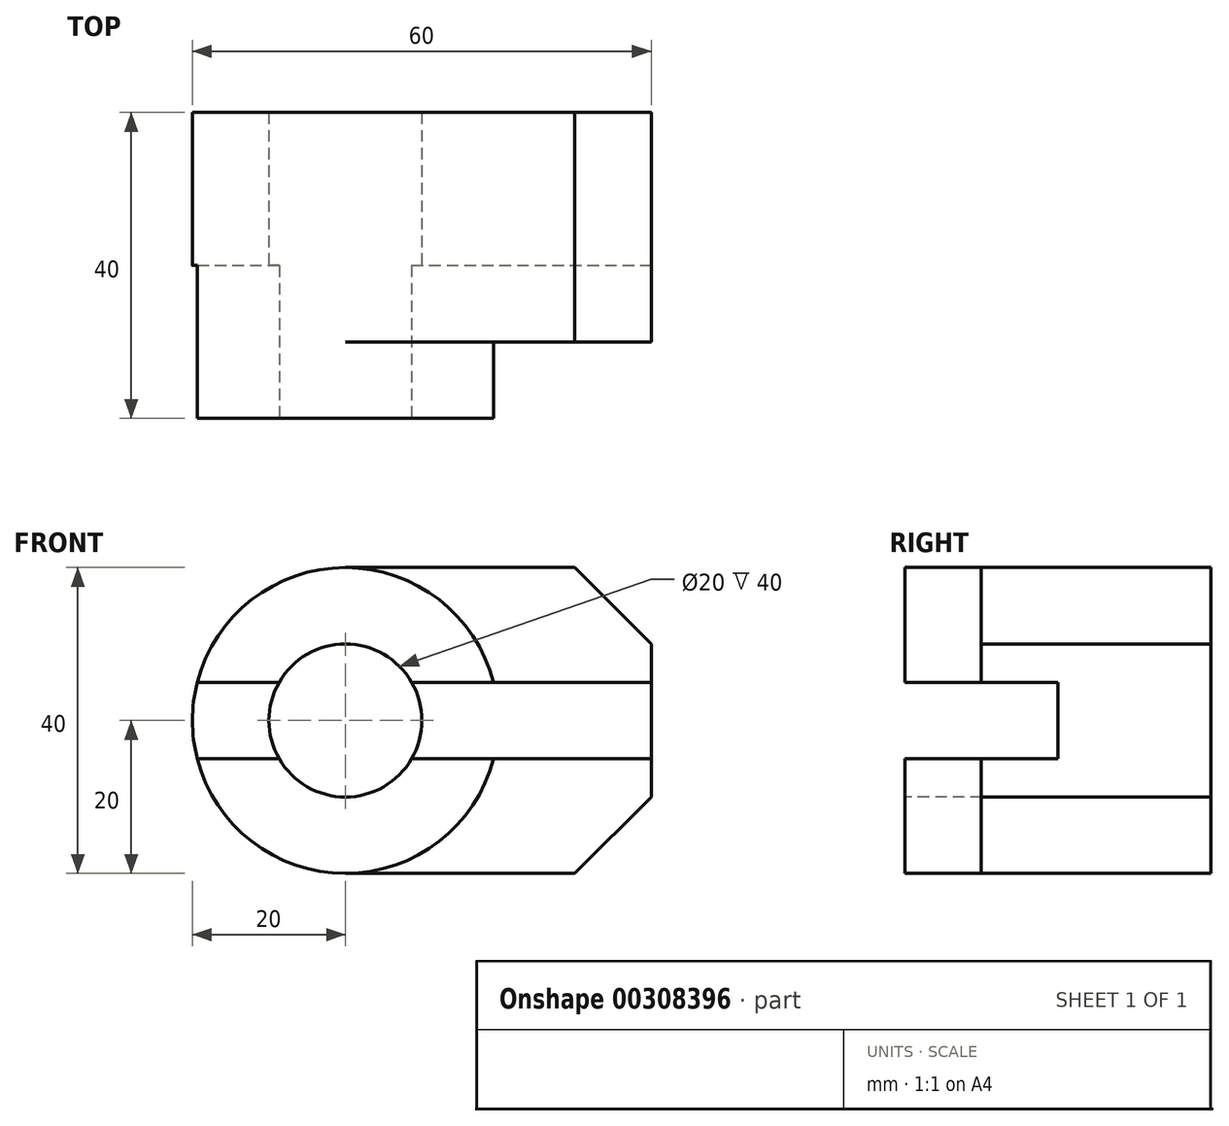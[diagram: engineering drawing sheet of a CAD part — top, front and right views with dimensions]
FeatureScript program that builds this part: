
annotation { "Feature Type Name" : "Feature", "Feature Type Description" : "" }
export const myFeature = defineFeature(function(context is Context, id is Id, definition is map)
    precondition{}
    {
        {
            var Q0;
            Q0=qCreatedBy(makeId("Front.planeOp"),FACE);
            var sketch = newSketch(context, id + "F0", { "sketchPlane" : qUnion([Q0])});
            skCircle(sketch, "E0", {"center": v(0, 0) * mm, "radius": 20 * mm});
            skSolve(sketch);
        }
        {
            var Q0;
            Q0=makeQuery(id+"F0.imprint","IMPRINT",FACE,{"disambiguationData":[TD([[makeQuery(id+"F0.imprint","IMPRINT",EDGE,{"derivedFrom":sQuery(id+"F0.wireOp",EDGE,"E0")}),1.0]])]});
            extrude(context, id + "F1", {"entities" : qUnion([Q0]), "depth" : 40 * mm});
        }
        {
            var Q0;
            Q0=makeQuery(id+"F1.opExtrude","CAP_FACE",FACE,{"disambiguationData":[OSD([sQuery(id+"F0.wireOp",EDGE,"E0")])],"isStart":true});
            var sketch = newSketch(context, id + "F2", { "sketchPlane" : qUnion([Q0])});
            skLineSegment(sketch, "E1", {"start": v(0, 20) * mm, "end": v(-30, 20) * mm});
            skLineSegment(sketch, "E2", {"start": v(-30, 20) * mm, "end": v(-40, 10) * mm});
            skLineSegment(sketch, "E3", {"start": v(-40, 10) * mm, "end": v(-40, -10) * mm});
            skLineSegment(sketch, "E4", {"start": v(-40, -10) * mm, "end": v(-30, -20) * mm});
            skLineSegment(sketch, "E5", {"start": v(-30, -20) * mm, "end": v(0, -20) * mm});
            skLineSegment(sketch, "E6", {"start": v(0, 0) * mm, "end": v(-40, 0) * mm, "construction": true});
            skSolve(sketch);
        }
        {
            var Q0;
            Q0 = qSketchRegion(id + "F2", true);
            var Q1;
            {var subQ0=sQuery(id+"F2.wireOp",EDGE,"E1");Q1=makeQuery(id+"F2.imprint","IMPRINT",FACE,{"disambiguationData":[TD([[makeQuery(id+"F2.imprint","IMPRINT",EDGE,{"derivedFrom":subQ0}),1.0]])]});}
            extrude(context, id + "F3", {"entities" : qUnion([Q0, Q1]), "operationType" : NewBodyOperationType.ADD, "oppositeDirection" : true, "depth" : 30 * mm});
        }
        {
            var Q0;
            Q0=makeQuery(id+"F1.opExtrude","CAP_FACE",FACE,{"disambiguationData":[OSD([sQuery(id+"F0.wireOp",EDGE,"E0")])],"isStart":false});
            var sketch = newSketch(context, id + "F4", { "sketchPlane" : qUnion([Q0])});
            skCircle(sketch, "E7", {"center": v(0, 0) * mm, "radius": 10 * mm});
            skSolve(sketch);
        }
        {
            var Q0;
            Q0 = qSketchRegion(id + "F4", true);
            extrude(context, id + "F5", {"entities" : qUnion([Q0]), "operationType" : NewBodyOperationType.REMOVE, "endBound" : BoundingType.THROUGH_ALL, "oppositeDirection" : true, "depth" : 25 * mm});
        }
        {
            var Q0;
            Q0=qCreatedBy(makeId("Right.planeOp"),FACE);
            var sketch = newSketch(context, id + "F6", { "sketchPlane" : qUnion([Q0])});
            skLineSegment(sketch, "E8", {"start": v(0, 0) * mm, "end": v(-40, 0) * mm, "construction": true});
            skLineSegment(sketch, "E9.bottom", {"start": v(-40, 5) * mm, "end": v(-20, 5) * mm});
            skLineSegment(sketch, "E9.top", {"start": v(-40, -5) * mm, "end": v(-20, -5) * mm});
            skLineSegment(sketch, "E9.left", {"start": v(-40, 5) * mm, "end": v(-40, -5) * mm});
            skLineSegment(sketch, "E9.right", {"start": v(-20, 5) * mm, "end": v(-20, -5) * mm});
            skSolve(sketch);
        }
        {
            var Q0;
            Q0 = qSketchRegion(id + "F6", true);
            extrude(context, id + "F7", {"entities" : qUnion([Q0]), "operationType" : NewBodyOperationType.REMOVE, "endBound" : BoundingType.THROUGH_ALL, "oppositeDirection" : true, "depth" : 25 * mm, "hasSecondDirection" : true, "secondDirectionBound" : SecondDirectionBoundingType.THROUGH_ALL, "secondDirectionOppositeDirection" : false, "secondDirectionDepth" : 25 * mm});
        }
    });
